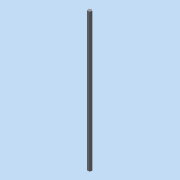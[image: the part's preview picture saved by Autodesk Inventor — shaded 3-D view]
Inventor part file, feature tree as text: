
AUTODESK INVENTOR PART (.ipt)
format: ipt  version: 2015 (Build 190159000, 159)  size: 66,048 bytes
history: native  units: in
note: dims shown in document units (in); Inventor stores cm internally (conversion verified against a paired STEP export)
features: extrude x1, sketch x1
ambient origin geometry x8: Origin, YZ Plane, XZ Plane, XY Plane, X Axis, Y Axis, Z Axis, Center Point
bodies: Solid1 (feature_tree)
feature tree (2):
  extrude  "Extrusion1"  [1 undecoded]
  sketch  "Sketch1"  dims[d1=7.0in d2=0.0in]
note: 1 required parameter value undecoded (feature->parameter linkage not recoverable at this tier; creation-order binding heuristic only, values carry confidence <= 0.55)
